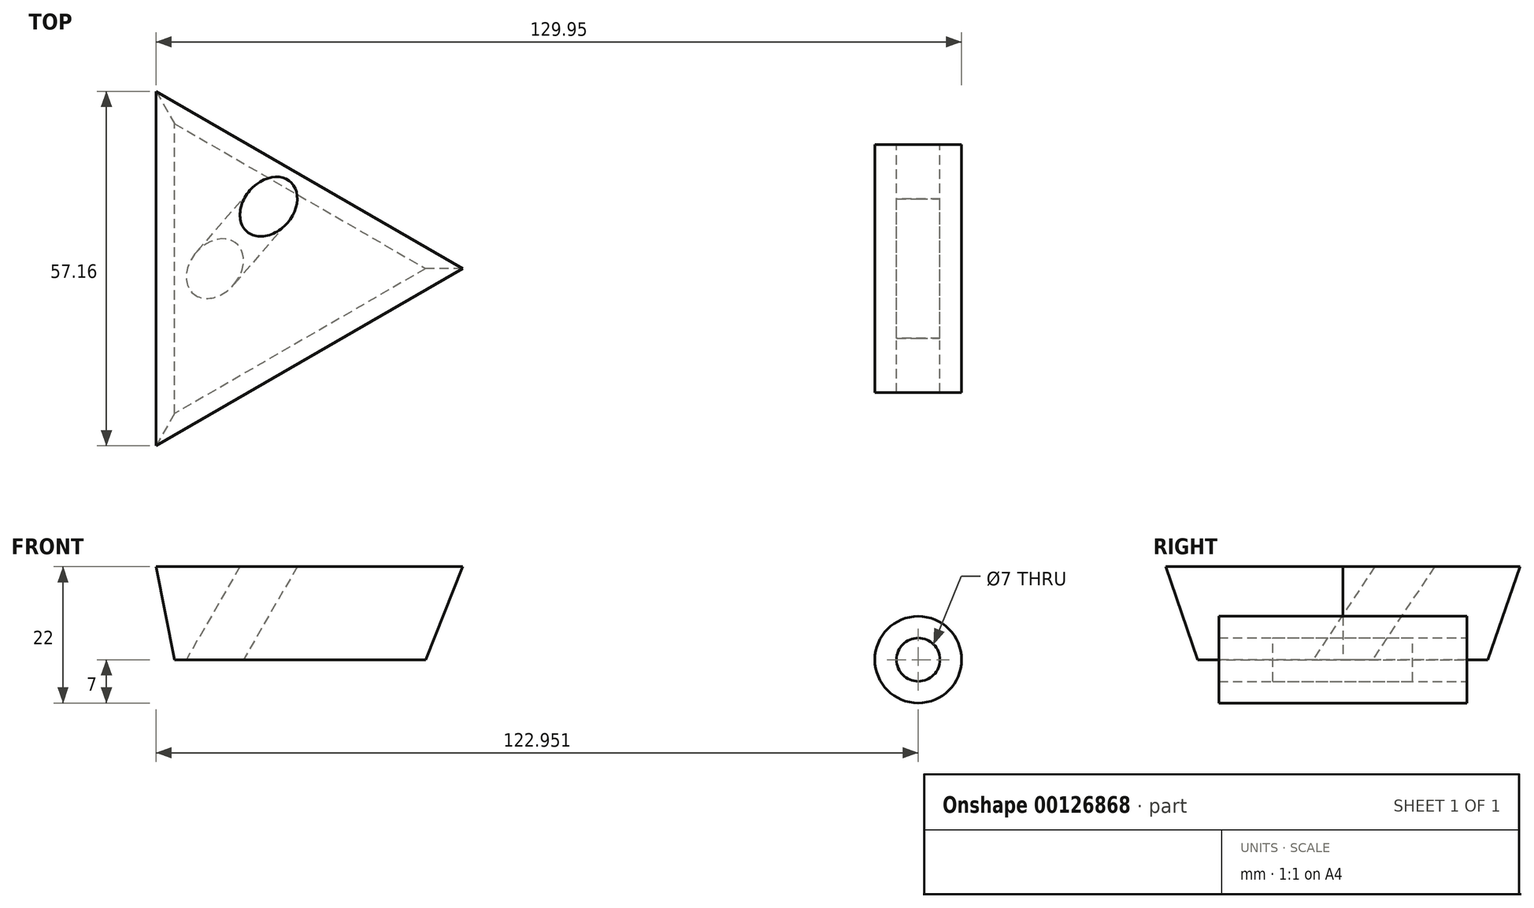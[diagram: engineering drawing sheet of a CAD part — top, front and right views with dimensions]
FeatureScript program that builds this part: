
annotation { "Feature Type Name" : "Feature", "Feature Type Description" : "" }
export const myFeature = defineFeature(function(context is Context, id is Id, definition is map)
    precondition{}
    {
        {
            assignVariable(context, id + "F0", {"name" : "strawlength", "anyValue" : 22.5});
        }
        {
            var Q0;
            Q0=qCreatedBy(makeId("Front.planeOp"),FACE);
            var sketch = newSketch(context, id + "F1", { "sketchPlane" : qUnion([Q0])});
            skCircle(sketch, "E0", {"center": v(106.45, 0) * mm, "radius": 3.5 * mm});
            skPoint(sketch, "E1", {"position": v(106.45, 3.5) * mm});
            skPoint(sketch, "E2", {"position": v(103.77, 2.25) * mm});
            skLineSegment(sketch, "E3", {"start": v(106.45, 0) * mm, "end": v(106.45, 3.5) * mm, "construction": true});
            skLineSegment(sketch, "E4", {"start": v(106.45, 0) * mm, "end": v(103.77, 2.25) * mm, "construction": true});
            skLineSegment(sketch, "E5", {"start": v(0, 0) * mm, "end": v(0, 74.77) * mm, "construction": true});
            skCircle(sketch, "E6", {"center": v(106.45, 0) * mm, "radius": 7 * mm});
            skSolve(sketch);
        }
        {
            var Q0;
            Q0=makeQuery(id+"F1.imprint","IMPRINT",FACE,{"disambiguationData":[TD([[makeQuery(id+"F1.imprint","IMPRINT",EDGE,{"derivedFrom":sQuery(id+"F1.wireOp",EDGE,"E0")}),1.0]])]});
            extrude(context, id + "F2", {"entities" : qUnion([Q0]), "endBound" : BoundingType.SYMMETRIC, "depth" : (getVariable(context, 'strawlength')) * mm});
        }
        {
            var Q0;
            Q0=qCreatedBy(makeId("Top.planeOp"),FACE);
            var sketch = newSketch(context, id + "F3", { "sketchPlane" : qUnion([Q0])});
            skCircle(sketch, "E7.cCircle", {"center": v(0, 0) * mm, "radius": 16.5 * mm, "construction": true});
            skLineSegment(sketch, "E7.0", {"start": v(-16.5, -28.58) * mm, "end": v(-16.5, 28.58) * mm});
            skLineSegment(sketch, "E7.1", {"start": v(-16.5, 28.58) * mm, "end": v(33, 0) * mm});
            skLineSegment(sketch, "E7.2", {"start": v(33, 0) * mm, "end": v(-16.5, -28.58) * mm});
            skPoint(sketch, "E7.0.midPoint", {"position": v(-16.5, 0) * mm});
            skCircle(sketch, "E8.cCircle", {"center": v(0, 0) * mm, "radius": 7 * mm, "construction": true});
            skLineSegment(sketch, "E8.0", {"start": v(-7, -12.12) * mm, "end": v(-7, 12.12) * mm});
            skLineSegment(sketch, "E8.1", {"start": v(-7, 12.12) * mm, "end": v(14, 0) * mm});
            skLineSegment(sketch, "E8.2", {"start": v(14, 0) * mm, "end": v(-7, -12.12) * mm});
            skPoint(sketch, "E8.0.midPoint", {"position": v(-7, 0) * mm});
            skSolve(sketch);
        }
        {
            var Q0;
            Q0=makeQuery(id+"F3.imprint","IMPRINT",FACE,{"disambiguationData":[TD([[makeQuery(id+"F3.imprint","IMPRINT",EDGE,{"derivedFrom":sQuery(id+"F3.wireOp",EDGE,"E7.0")}),-1.0]])]});
            var Q1;
            Q1=makeQuery(id+"F3.imprint","IMPRINT",FACE,{"disambiguationData":[TD([[makeQuery(id+"F3.imprint","IMPRINT",EDGE,{"derivedFrom":sQuery(id+"F3.wireOp",EDGE,"E8.0")}),-1.0]])]});
            extrude(context, id + "F4", {"entities" : qUnion([Q0, Q1]), "depth" : 15 * mm});
        }
        {
            var Q0;
            Q0=sQuery(id+"F3.wireOp",EDGE,"E8.0");
            var Q1;
            Q1=qCreatedBy(makeId("Top.planeOp"),FACE);
            cPlane(context, id + "F5", {"entities" : qUnion([Q0, Q1]), "cplaneType" : CPlaneType.LINE_ANGLE, "offset" : mm, "angle" : 30 * degree, "width" : 150 * mm, "height" : 150 * mm});
        }
        {
            var Q0;
            Q0=qCreatedBy(id+"F5.planeOp",FACE);
            var sketch = newSketch(context, id + "F6", { "sketchPlane" : qUnion([Q0])});
            skLineSegment(sketch, "E9", {"start": v(0, 11.7) * mm, "end": v(0, -17.07) * mm, "construction": true});
            skLineSegment(sketch, "E10", {"start": v(0, 0) * mm, "end": v(-11.58, 0) * mm, "construction": true});
            skSolve(sketch);
        }
        {
            var Q0;
            Q0=qCreatedBy(id+"F5.planeOp",FACE);
            var Q1;
            Q1=sQuery(id+"F6.wireOp",EDGE,"E10");
            cPlane(context, id + "F7", {"entities" : qUnion([Q0, Q1]), "cplaneType" : CPlaneType.LINE_ANGLE, "offset" : 25 * mm, "angle" : 30 * degree, "width" : 150 * mm, "height" : 150 * mm});
        }
        {
            var Q0;
            Q0=qCreatedBy(id+"F7.planeOp",FACE);
            var sketch = newSketch(context, id + "F8", { "sketchPlane" : qUnion([Q0])});
            skPoint(sketch, "E11", {"position": v(-6.3, 0) * mm});
            skCircle(sketch, "E12", {"center": v(-6.3, 0) * mm, "radius": 4 * mm});
            skSolve(sketch);
        }
        {
            var Q0;
            Q0 = qSketchRegion(id + "F8", true);
            extrude(context, id + "F9", {"entities" : qUnion([Q0]), "operationType" : NewBodyOperationType.REMOVE, "endBound" : BoundingType.SYMMETRIC, "depth" : 1100 * mm});
        }
        {
            var Q0;
            Q0=makeQuery(id+"F4.opExtrude","CAP_EDGE",EDGE,{"disambiguationData":[OSD([sQuery(id+"F3.wireOp",EDGE,"E7.0")])],"isStart":true});
            var Q1;
            Q1=makeQuery(id+"F4.opExtrude","CAP_EDGE",EDGE,{"disambiguationData":[OSD([sQuery(id+"F3.wireOp",EDGE,"E7.1")])],"isStart":true});
            var Q2;
            Q2=makeQuery(id+"F4.opExtrude","CAP_EDGE",EDGE,{"disambiguationData":[OSD([sQuery(id+"F3.wireOp",EDGE,"E7.2")])],"isStart":true});
            chamfer(context, id + "F10", {"entities" : qUnion([Q0, Q1, Q2]), "chamferType" : ChamferType.TWO_OFFSETS, "width1" : 3 * mm, "oppositeDirection" : false, "width2" : 15 * mm, "tangentPropagation" : true});
        }
        {
            var Q0;
            Q0=makeQuery(id+"F1.imprint","IMPRINT",FACE,{"disambiguationData":[TD([[makeQuery(id+"F1.imprint","IMPRINT",EDGE,{"derivedFrom":sQuery(id+"F1.wireOp",EDGE,"E0")}),-1.0]])]});
            extrude(context, id + "F11", {"entities" : qUnion([Q0]), "endBound" : BoundingType.SYMMETRIC, "depth" : 40 * mm});
        }
    });
